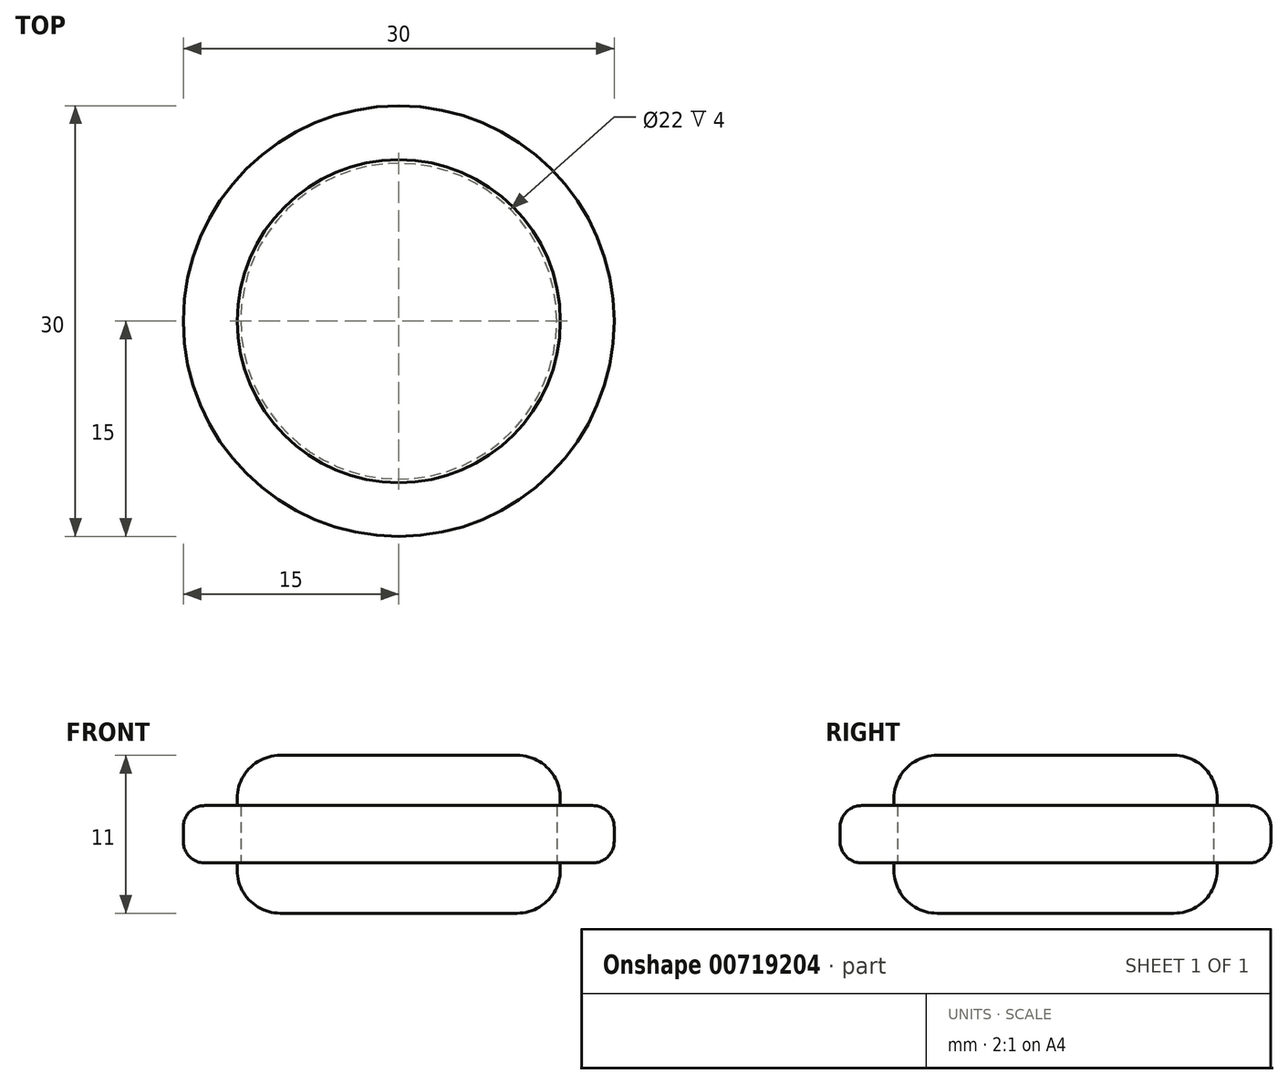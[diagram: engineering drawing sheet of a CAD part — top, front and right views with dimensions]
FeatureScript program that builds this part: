
annotation { "Feature Type Name" : "Feature", "Feature Type Description" : "" }
export const myFeature = defineFeature(function(context is Context, id is Id, definition is map)
    precondition{}
    {
        {
            assignVariable(context, id + "F0", {"name" : "depth", "anyValue" : 4 * mm});
        }
        {
            assignVariable(context, id + "F1", {"name" : "height", "anyValue" : 11 * mm});
        }
        {
            var Q0;
            Q0=qCreatedBy(makeId("Top.planeOp"),FACE);
            var sketch = newSketch(context, id + "F2", { "sketchPlane" : qUnion([Q0])});
            skCircle(sketch, "E0", {"center": v(0, 0) * mm, "radius": 15 * mm});
            skCircle(sketch, "E1", {"center": v(0, 0) * mm, "radius": 11 * mm});
            skSolve(sketch);
        }
        {
            var Q0;
            Q0=makeQuery(id+"F2.imprint","IMPRINT",FACE,{"disambiguationData":[TD([[makeQuery(id+"F2.imprint","IMPRINT",EDGE,{"derivedFrom":sQuery(id+"F2.wireOp",EDGE,"E0")}),1.0]])]});
            extrude(context, id + "F3", {"entities" : qUnion([Q0]), "endBound" : BoundingType.SYMMETRIC, "depth" : getVariable(context, 'depth'), "offsetDistance" : 25 * mm});
        }
        {
            var Q0;
            Q0=qCreatedBy(makeId("Top.planeOp"),FACE);
            var sketch = newSketch(context, id + "F4", { "sketchPlane" : qUnion([Q0])});
            skCircle(sketch, "E2", {"center": v(0, 0) * mm, "radius": 11.25 * mm});
            skSolve(sketch);
        }
        {
            var Q0;
            Q0=qSketchRegion(id+"F4",true);
            extrude(context, id + "F5", {"entities" : qUnion([Q0]), "endBound" : BoundingType.SYMMETRIC, "depth" : getVariable(context, 'height'), "offsetDistance" : 25 * mm});
        }
        {
            var Q0;
            Q0=makeQuery(id+"F5.opExtrude","CAP_FACE",FACE,{"disambiguationData":[OSD([sQuery(id+"F4.wireOp",EDGE,"E2")])],"isStart":false});
            var Q1;
            Q1=makeQuery(id+"F5.opExtrude","CAP_FACE",FACE,{"disambiguationData":[OSD([sQuery(id+"F4.wireOp",EDGE,"E2")])],"isStart":true});
            fillet(context, id + "F6", {"entities" : qUnion([Q0, Q1]), "radius" : 3 * mm, "tangentPropagation" : true, "allowEdgeOverflow" : false});
        }
        {
            var Q0;
            Q0=makeQuery(id+"F3.opExtrude","SWEPT_BODY",BODY,{"disambiguationData":[OSD([sQuery(id+"F2.wireOp",EDGE,"E0"),sQuery(id+"F2.wireOp",EDGE,"E1")])]});
            transform(context, id + "F7", {"entities" : qUnion([Q0]), "transformType" : TransformType.TRANSLATION_3D, "dx" : 0 * mm, "dy" : 0 * mm, "dz" : 0 * mm, "makeCopy" : true});
        }
        {
            var Q0;
            Q0=makeQuery(id+"F7.opPattern","COPY",BODY,{"derivedFrom":makeQuery(id+"F3.opExtrude","SWEPT_BODY",BODY,{"disambiguationData":[OSD([sQuery(id+"F2.wireOp",EDGE,"E0"),sQuery(id+"F2.wireOp",EDGE,"E1")])]}),"instanceName":"1"});
            var Q1;
            Q1=makeQuery(id+"F5.opExtrude","SWEPT_BODY",BODY,{"disambiguationData":[OSD([sQuery(id+"F4.wireOp",EDGE,"E2")])]});
            booleanBodies(context, id + "F8", {"operationType" : BooleanOperationType.SUBTRACTION, "tools" : qUnion([Q0]), "targets" : qUnion([Q1])});
        }
        {
            var Q0;
            Q0=makeQuery(id+"F3.opExtrude","SWEPT_FACE",FACE,{"disambiguationData":[OSD([sQuery(id+"F2.wireOp",EDGE,"E0")])]});
            fillet(context, id + "F9", {"entities" : qUnion([Q0]), "radius" : 1.5 * mm, "tangentPropagation" : true, "allowEdgeOverflow" : false});
        }
    });
